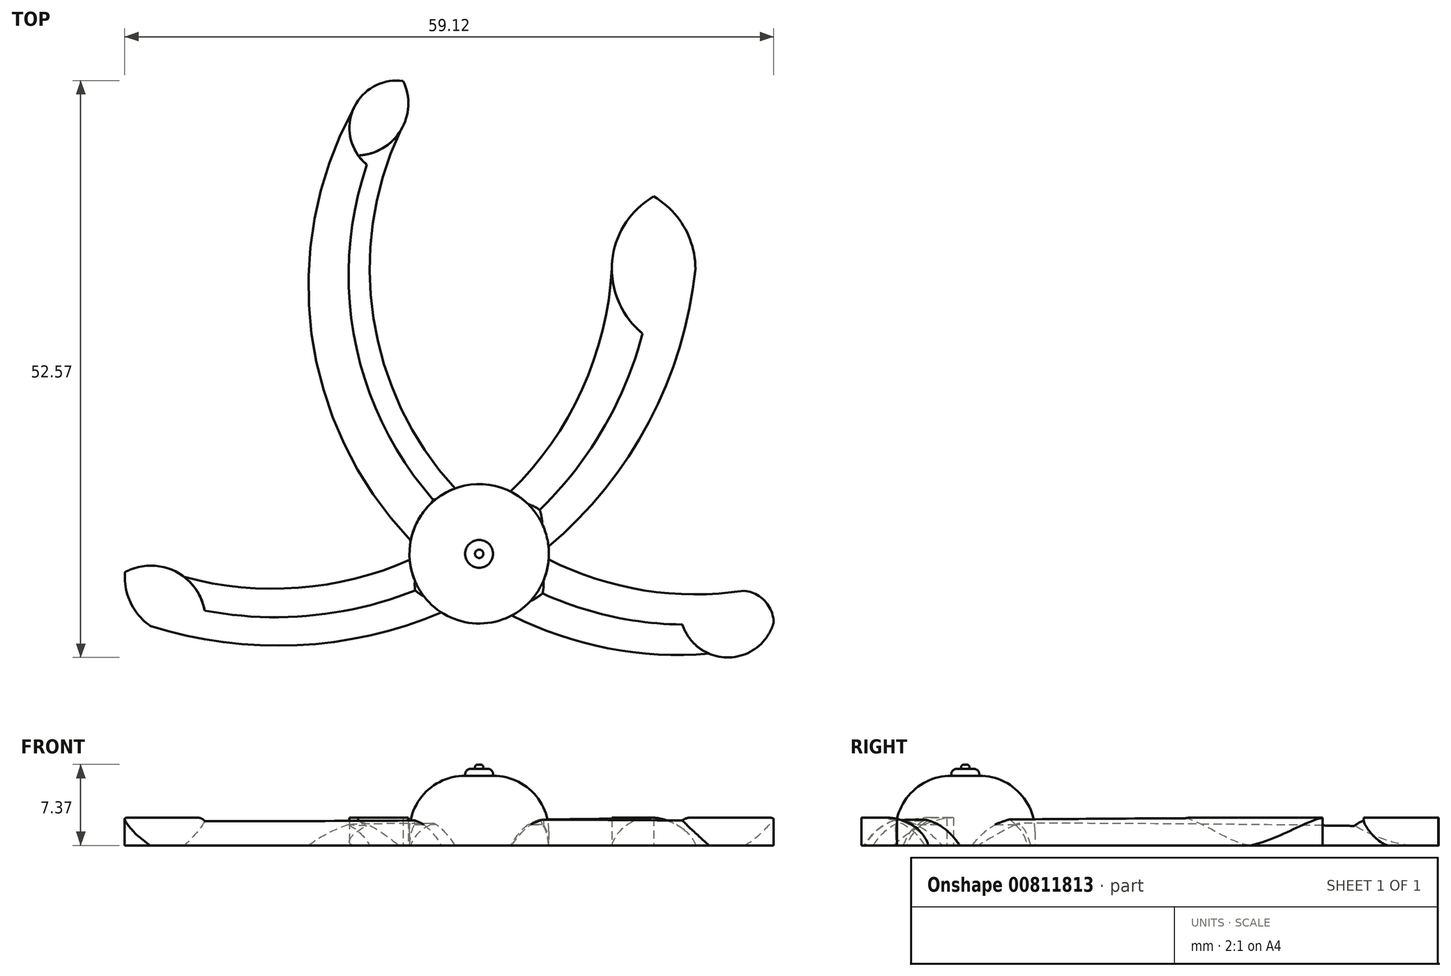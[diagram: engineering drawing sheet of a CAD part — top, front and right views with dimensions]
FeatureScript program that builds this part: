
annotation { "Feature Type Name" : "Feature", "Feature Type Description" : "" }
export const myFeature = defineFeature(function(context is Context, id is Id, definition is map)
    precondition{}
    {
        {
            var Q0;
            Q0=qCreatedBy(makeId("Top.planeOp"),FACE);
            var sketch = newSketch(context, id + "F0", { "sketchPlane" : qUnion([Q0])});
            skArc(sketch, "E0", {"start": v(-15.38, 23.36) * mm, "mid": v(-14.05, -11.17) * mm, "end": v(17, -26.35) * mm});
            skArc(sketch, "E1", {"start": v(-11.14, 21.25) * mm, "mid": v(-8.01, -9.06) * mm, "end": v(20.18, -20.62) * mm});
            skArc(sketch, "E2", {"start": v(-33.9, -23.82) * mm, "mid": v(-1.34, -19.37) * mm, "end": v(15.74, 8.71) * mm});
            skArc(sketch, "E3", {"start": v(-30.82, -19.37) * mm, "mid": v(-4.66, -14.6) * mm, "end": v(8.13, 8.71) * mm});
            skPoint(sketch, "E3.startSnap0", {"position": v(-1.34, -19.37) * mm});
            skCircle(sketch, "E4", {"center": v(-3.95, -17.25) * mm, "radius": 6.35 * mm});
            skLineSegment(sketch, "E5", {"start": v(-11.14, 21.25) * mm, "end": v(-15.38, 23.36) * mm});
            skLineSegment(sketch, "E6", {"start": v(8.13, 8.71) * mm, "end": v(15.74, 8.71) * mm});
            skLineSegment(sketch, "E7", {"start": v(20.18, -20.62) * mm, "end": v(17, -26.35) * mm});
            skLineSegment(sketch, "E8", {"start": v(-30.82, -19.37) * mm, "end": v(-33.9, -23.82) * mm});
            skLineSegment(sketch, "E9", {"start": v(11.94, 8.71) * mm, "end": v(11.94, 15.3) * mm});
            skArc(sketch, "E10", {"start": v(11.94, 15.3) * mm, "mid": v(9.15, 12.52) * mm, "end": v(8.13, 8.71) * mm});
            skArc(sketch, "E11", {"start": v(15.74, 8.71) * mm, "mid": v(14.72, 12.52) * mm, "end": v(11.94, 15.3) * mm});
            skLineSegment(sketch, "E12", {"start": v(-13.26, 22.3) * mm, "end": v(-10.87, 25.83) * mm});
            skArc(sketch, "E13", {"start": v(-10.87, 25.83) * mm, "mid": v(-13.53, 25.34) * mm, "end": v(-15.38, 23.36) * mm});
            skArc(sketch, "E14", {"start": v(-11.14, 21.25) * mm, "mid": v(-10.42, 23.5) * mm, "end": v(-10.87, 25.83) * mm});
            skLineSegment(sketch, "E15", {"start": v(-32.36, -21.6) * mm, "end": v(-36.22, -18.92) * mm});
            skArc(sketch, "E16", {"start": v(-36.22, -18.92) * mm, "mid": v(-35.72, -21.68) * mm, "end": v(-33.9, -23.82) * mm});
            skArc(sketch, "E17", {"start": v(-30.82, -19.37) * mm, "mid": v(-33.45, -18.35) * mm, "end": v(-36.22, -18.92) * mm});
            skLineSegment(sketch, "E18", {"start": v(18.58, -23.48) * mm, "end": v(22.88, -23.48) * mm});
            skArc(sketch, "E19", {"start": v(17, -26.35) * mm, "mid": v(20.59, -26.26) * mm, "end": v(22.88, -23.48) * mm});
            skArc(sketch, "E20", {"start": v(22.88, -23.48) * mm, "mid": v(22.06, -21.54) * mm, "end": v(20.18, -20.62) * mm});
            skSolve(sketch);
        }
        {
            var Q0;
            {var subQ0=sQuery(id+"F0.wireOp",EDGE,"E5");Q0=makeQuery(id+"F0.imprint","IMPRINT",FACE,{"disambiguationData":[TD([[makeQuery(id+"F0.imprint","IMPRINT",EDGE,{"derivedFrom":subQ0}),1.0]])]});}
            var Q1;
            {var subQ0=sQuery(id+"F0.wireOp",EDGE,"E7");Q1=makeQuery(id+"F0.imprint","IMPRINT",FACE,{"disambiguationData":[TD([[makeQuery(id+"F0.imprint","IMPRINT",EDGE,{"derivedFrom":subQ0}),-1.0]])]});}
            var Q2;
            {var subQ0=sQuery(id+"F0.wireOp",EDGE,"E8");Q2=makeQuery(id+"F0.imprint","IMPRINT",FACE,{"disambiguationData":[TD([[makeQuery(id+"F0.imprint","IMPRINT",EDGE,{"derivedFrom":subQ0}),1.0]])]});}
            var Q3;
            {var subQ0=sQuery(id+"F0.wireOp",EDGE,"E6");Q3=makeQuery(id+"F0.imprint","IMPRINT",FACE,{"disambiguationData":[TD([[makeQuery(id+"F0.imprint","IMPRINT",EDGE,{"derivedFrom":subQ0}),-1.0]])]});}
            var Q4;
            {var subQ2=sQuery(id+"F0.wireOp",EDGE,"E15");Q4=makeQuery(id+"F0.imprint","IMPRINT",FACE,{"disambiguationData":[TD([[makeQuery(id+"F0.imprint","IMPRINT",EDGE,{"derivedFrom":subQ2}),-1.0]])]});}
            var Q5;
            {var subQ2=sQuery(id+"F0.wireOp",EDGE,"E15");Q5=makeQuery(id+"F0.imprint","IMPRINT",FACE,{"disambiguationData":[TD([[makeQuery(id+"F0.imprint","IMPRINT",EDGE,{"derivedFrom":subQ2}),1.0]])]});}
            var Q6;
            {var subQ2=sQuery(id+"F0.wireOp",EDGE,"E12");Q6=makeQuery(id+"F0.imprint","IMPRINT",FACE,{"disambiguationData":[TD([[makeQuery(id+"F0.imprint","IMPRINT",EDGE,{"derivedFrom":subQ2}),1.0]])]});}
            var Q7;
            {var subQ2=sQuery(id+"F0.wireOp",EDGE,"E12");Q7=makeQuery(id+"F0.imprint","IMPRINT",FACE,{"disambiguationData":[TD([[makeQuery(id+"F0.imprint","IMPRINT",EDGE,{"derivedFrom":subQ2}),-1.0]])]});}
            var Q8;
            {var subQ2=sQuery(id+"F0.wireOp",EDGE,"E9");Q8=makeQuery(id+"F0.imprint","IMPRINT",FACE,{"disambiguationData":[TD([[makeQuery(id+"F0.imprint","IMPRINT",EDGE,{"derivedFrom":subQ2}),1.0]])]});}
            var Q9;
            {var subQ2=sQuery(id+"F0.wireOp",EDGE,"E9");Q9=makeQuery(id+"F0.imprint","IMPRINT",FACE,{"disambiguationData":[TD([[makeQuery(id+"F0.imprint","IMPRINT",EDGE,{"derivedFrom":subQ2}),-1.0]])]});}
            var Q10;
            {var subQ2=sQuery(id+"F0.wireOp",EDGE,"E18");Q10=makeQuery(id+"F0.imprint","IMPRINT",FACE,{"disambiguationData":[TD([[makeQuery(id+"F0.imprint","IMPRINT",EDGE,{"derivedFrom":subQ2}),1.0]])]});}
            var Q11;
            {var subQ2=sQuery(id+"F0.wireOp",EDGE,"E18");Q11=makeQuery(id+"F0.imprint","IMPRINT",FACE,{"disambiguationData":[TD([[makeQuery(id+"F0.imprint","IMPRINT",EDGE,{"derivedFrom":subQ2}),-1.0]])]});}
            extrude(context, id + "F1", {"entities" : qUnion([Q0, Q1, Q2, Q3, Q4, Q5, Q6, Q7, Q8, Q9, Q10, Q11]), "depth" : 2.54 * mm, "offsetDistance" : 25.4 * mm});
        }
        {
            var Q0;
            {var subQ0=sQuery(id+"F0.wireOp",EDGE,"E4");var subQ1=sQuery(id+"F0.wireOp",EDGE,"E0");var subQ2=makeQuery(id+"F0.imprint","INTERSECT",VERTEX,{"disambiguationData":[OD(0.0)],"derivedFrom":[subQ1,subQ0]});Q0=makeQuery(id+"F0.imprint","IMPRINT",FACE,{"disambiguationData":[TD([[makeQuery(id+"F0.imprint","IMPRINT",EDGE,{"disambiguationData":[TD([[subQ2,-1.0]])],"derivedFrom":subQ1}),1.0]])]});}
            var Q1;
            {var subQ0=sQuery(id+"F0.wireOp",EDGE,"E4");var subQ1=sQuery(id+"F0.wireOp",EDGE,"E0");var subQ2=makeQuery(id+"F0.imprint","INTERSECT",VERTEX,{"disambiguationData":[OD(0.0)],"derivedFrom":[subQ1,subQ0]});Q1=makeQuery(id+"F0.imprint","IMPRINT",FACE,{"disambiguationData":[TD([[makeQuery(id+"F0.imprint","IMPRINT",EDGE,{"disambiguationData":[TD([[subQ2,-1.0]])],"derivedFrom":subQ1}),-1.0]])]});}
            var Q2;
            {var subQ0=sQuery(id+"F0.wireOp",EDGE,"E4");var subQ1=sQuery(id+"F0.wireOp",EDGE,"E1");var subQ2=makeQuery(id+"F0.imprint","INTERSECT",VERTEX,{"disambiguationData":[OD(1.0)],"derivedFrom":[subQ1,subQ0]});Q2=makeQuery(id+"F0.imprint","IMPRINT",FACE,{"disambiguationData":[TD([[makeQuery(id+"F0.imprint","IMPRINT",EDGE,{"disambiguationData":[TD([[subQ2,1.0]])],"derivedFrom":subQ1}),1.0]])]});}
            var Q3;
            {var subQ0=sQuery(id+"F0.wireOp",EDGE,"E4");var subQ1=sQuery(id+"F0.wireOp",EDGE,"E0");var subQ2=makeQuery(id+"F0.imprint","INTERSECT",VERTEX,{"disambiguationData":[OD(1.0)],"derivedFrom":[subQ1,subQ0]});Q3=makeQuery(id+"F0.imprint","IMPRINT",FACE,{"disambiguationData":[TD([[makeQuery(id+"F0.imprint","IMPRINT",EDGE,{"disambiguationData":[TD([[subQ2,1.0]])],"derivedFrom":subQ1}),-1.0]])]});}
            var Q4;
            {var subQ0=sQuery(id+"F0.wireOp",EDGE,"E3");var subQ1=sQuery(id+"F0.wireOp",EDGE,"E0");var subQ2=makeQuery(id+"F0.imprint","INTERSECT",VERTEX,{"derivedFrom":[subQ1,subQ0]});Q4=makeQuery(id+"F0.imprint","IMPRINT",FACE,{"disambiguationData":[TD([[makeQuery(id+"F0.imprint","IMPRINT",EDGE,{"disambiguationData":[TD([[subQ2,-1.0]])],"derivedFrom":subQ1}),1.0]])]});}
            var Q5;
            {var subQ0=sQuery(id+"F0.wireOp",EDGE,"E3");var subQ1=sQuery(id+"F0.wireOp",EDGE,"E0");var subQ2=makeQuery(id+"F0.imprint","INTERSECT",VERTEX,{"derivedFrom":[subQ1,subQ0]});Q5=makeQuery(id+"F0.imprint","IMPRINT",FACE,{"disambiguationData":[TD([[makeQuery(id+"F0.imprint","IMPRINT",EDGE,{"disambiguationData":[TD([[subQ2,-1.0]])],"derivedFrom":subQ1}),-1.0]])]});}
            var Q6;
            {var subQ0=sQuery(id+"F0.wireOp",EDGE,"E4");var subQ1=sQuery(id+"F0.wireOp",EDGE,"E1");var subQ2=makeQuery(id+"F0.imprint","INTERSECT",VERTEX,{"disambiguationData":[OD(0.0)],"derivedFrom":[subQ1,subQ0]});Q6=makeQuery(id+"F0.imprint","IMPRINT",FACE,{"disambiguationData":[TD([[makeQuery(id+"F0.imprint","IMPRINT",EDGE,{"disambiguationData":[TD([[subQ2,-1.0]])],"derivedFrom":subQ1}),1.0]])]});}
            var Q7;
            {var subQ0=sQuery(id+"F0.wireOp",EDGE,"E3");var subQ1=sQuery(id+"F0.wireOp",EDGE,"E1");var subQ2=makeQuery(id+"F0.imprint","INTERSECT",VERTEX,{"derivedFrom":[subQ1,subQ0]});Q7=makeQuery(id+"F0.imprint","IMPRINT",FACE,{"disambiguationData":[TD([[makeQuery(id+"F0.imprint","IMPRINT",EDGE,{"disambiguationData":[TD([[subQ2,-1.0]])],"derivedFrom":subQ1}),1.0]])]});}
            var Q8;
            {var subQ0=sQuery(id+"F0.wireOp",EDGE,"E4");var subQ1=sQuery(id+"F0.wireOp",EDGE,"E0");var subQ2=makeQuery(id+"F0.imprint","INTERSECT",VERTEX,{"disambiguationData":[OD(1.0)],"derivedFrom":[subQ1,subQ0]});Q8=makeQuery(id+"F0.imprint","IMPRINT",FACE,{"disambiguationData":[TD([[makeQuery(id+"F0.imprint","IMPRINT",EDGE,{"disambiguationData":[TD([[subQ2,1.0]])],"derivedFrom":subQ1}),1.0]])]});}
            extrude(context, id + "F2", {"entities" : qUnion([Q0, Q1, Q2, Q3, Q4, Q5, Q6, Q7, Q8]), "depth" : 6.35 * mm, "offsetDistance" : 25.4 * mm});
        }
        {
            var Q0;
            Q0=makeQuery(id+"F2.opExtrude","CAP_EDGE",EDGE,{"disambiguationData":[OSD([sQuery(id+"F0.wireOp",EDGE,"E4")])],"isStart":false});
            fillet(context, id + "F3", {"entities" : qUnion([Q0]), "radius" : 5.08 * mm, "tangentPropagation" : true, "allowEdgeOverflow" : false});
        }
        {
            var Q0;
            {var subQ0=sQuery(id+"F0.wireOp",EDGE,"E4");Q0=makeQuery(id+"F1.opExtrude","CAP_EDGE",EDGE,{"disambiguationData":[OSD([subQ0]),TDD([makeQuery(id+"F0.imprint","IMPRINT",EDGE,{"disambiguationData":[TD([[makeQuery(id+"F0.imprint","INTERSECT",VERTEX,{"disambiguationData":[OD(0.0)],"derivedFrom":[sQuery(id+"F0.wireOp",EDGE,"E2"),subQ0]}),1.0]])],"derivedFrom":subQ0})])],"isStart":false});}
            chamfer(context, id + "F4", {"entities" : qUnion([Q0]), "width" : 0.64 * mm, "tangentPropagation" : true});
        }
        {
            var Q0;
            {var subQ0=sQuery(id+"F0.wireOp",EDGE,"E4");Q0=makeQuery(id+"F1.opExtrude","CAP_EDGE",EDGE,{"disambiguationData":[OSD([subQ0]),TDD([makeQuery(id+"F0.imprint","IMPRINT",EDGE,{"disambiguationData":[TD([[makeQuery(id+"F0.imprint","INTERSECT",VERTEX,{"disambiguationData":[OD(0.0)],"derivedFrom":[sQuery(id+"F0.wireOp",EDGE,"E0"),subQ0]}),1.0]])],"derivedFrom":subQ0})])],"isStart":false});}
            chamfer(context, id + "F5", {"entities" : qUnion([Q0]), "width" : 0.64 * mm, "tangentPropagation" : true});
        }
        {
            var Q0;
            {var subQ0=sQuery(id+"F0.wireOp",EDGE,"E4");Q0=makeQuery(id+"F1.opExtrude","CAP_EDGE",EDGE,{"disambiguationData":[OSD([subQ0]),TDD([makeQuery(id+"F0.imprint","IMPRINT",EDGE,{"disambiguationData":[TD([[makeQuery(id+"F0.imprint","INTERSECT",VERTEX,{"disambiguationData":[OD(1.0)],"derivedFrom":[sQuery(id+"F0.wireOp",EDGE,"E0"),subQ0]}),-1.0]])],"derivedFrom":subQ0})])],"isStart":false});}
            chamfer(context, id + "F6", {"entities" : qUnion([Q0]), "width" : 0.64 * mm, "tangentPropagation" : true});
        }
        {
            var Q0;
            {var subQ0=sQuery(id+"F0.wireOp",EDGE,"E4");Q0=makeQuery(id+"F1.opExtrude","CAP_EDGE",EDGE,{"disambiguationData":[OSD([subQ0]),TDD([makeQuery(id+"F0.imprint","IMPRINT",EDGE,{"disambiguationData":[TD([[makeQuery(id+"F0.imprint","INTERSECT",VERTEX,{"disambiguationData":[OD(1.0)],"derivedFrom":[sQuery(id+"F0.wireOp",EDGE,"E2"),subQ0]}),-1.0]])],"derivedFrom":subQ0})])],"isStart":false});}
            chamfer(context, id + "F7", {"entities" : qUnion([Q0]), "width" : 0.64 * mm, "tangentPropagation" : true});
        }
        {
            var Q0;
            {var subQ0=sQuery(id+"F0.wireOp",EDGE,"E3");Q0=makeQuery(id+"F1.opExtrude","CAP_EDGE",EDGE,{"disambiguationData":[OSD([subQ0]),TDD([makeQuery(id+"F0.imprint","IMPRINT",EDGE,{"disambiguationData":[TD([[makeQuery(id+"F0.imprint","INTERSECT",VERTEX,{"derivedFrom":[subQ0,sQuery(id+"F0.wireOp",EDGE,"E6")]}),1.0]])],"derivedFrom":subQ0})])],"isStart":false});}
            fillet(context, id + "F8", {"entities" : qUnion([Q0]), "radius" : 5.08 * mm, "tangentPropagation" : true, "allowEdgeOverflow" : false});
        }
        {
            var Q0;
            {var subQ0=sQuery(id+"F0.wireOp",EDGE,"E2");Q0=makeQuery(id+"F1.opExtrude","CAP_EDGE",EDGE,{"disambiguationData":[OSD([subQ0]),TDD([makeQuery(id+"F0.imprint","IMPRINT",EDGE,{"disambiguationData":[TD([[makeQuery(id+"F0.imprint","INTERSECT",VERTEX,{"derivedFrom":[subQ0,sQuery(id+"F0.wireOp",EDGE,"E6")]}),1.0]])],"derivedFrom":subQ0})])],"isStart":false});}
            fillet(context, id + "F9", {"entities" : qUnion([Q0]), "radius" : 5.08 * mm, "tangentPropagation" : true, "allowEdgeOverflow" : false});
        }
        {
            var Q0;
            {var subQ0=sQuery(id+"F0.wireOp",EDGE,"E1");Q0=makeQuery(id+"F1.opExtrude","CAP_EDGE",EDGE,{"disambiguationData":[OSD([subQ0]),TDD([makeQuery(id+"F0.imprint","IMPRINT",EDGE,{"disambiguationData":[TD([[makeQuery(id+"F0.imprint","INTERSECT",VERTEX,{"derivedFrom":[subQ0,sQuery(id+"F0.wireOp",EDGE,"E5")]}),-1.0]])],"derivedFrom":subQ0})])],"isStart":false});}
            fillet(context, id + "F10", {"entities" : qUnion([Q0]), "radius" : 5.08 * mm, "tangentPropagation" : true, "allowEdgeOverflow" : false});
        }
        {
            var Q0;
            {var subQ0=sQuery(id+"F0.wireOp",EDGE,"E3");Q0=makeQuery(id+"F1.opExtrude","CAP_EDGE",EDGE,{"disambiguationData":[OSD([subQ0]),TDD([makeQuery(id+"F0.imprint","IMPRINT",EDGE,{"disambiguationData":[TD([[makeQuery(id+"F0.imprint","INTERSECT",VERTEX,{"derivedFrom":[subQ0,sQuery(id+"F0.wireOp",EDGE,"E8")]}),-1.0]])],"derivedFrom":subQ0})])],"isStart":false});}
            fillet(context, id + "F11", {"entities" : qUnion([Q0]), "radius" : 5.08 * mm, "tangentPropagation" : true, "allowEdgeOverflow" : false});
        }
        {
            var Q0;
            {var subQ0=sQuery(id+"F0.wireOp",EDGE,"E2");Q0=makeQuery(id+"F1.opExtrude","CAP_EDGE",EDGE,{"disambiguationData":[OSD([subQ0]),TDD([makeQuery(id+"F0.imprint","IMPRINT",EDGE,{"disambiguationData":[TD([[makeQuery(id+"F0.imprint","INTERSECT",VERTEX,{"derivedFrom":[subQ0,sQuery(id+"F0.wireOp",EDGE,"E8")]}),-1.0]])],"derivedFrom":subQ0})])],"isStart":false});}
            fillet(context, id + "F12", {"entities" : qUnion([Q0]), "radius" : 5.08 * mm, "tangentPropagation" : true, "allowEdgeOverflow" : false});
        }
        {
            var Q0;
            {var subQ0=sQuery(id+"F0.wireOp",EDGE,"E0");Q0=makeQuery(id+"F1.opExtrude","CAP_EDGE",EDGE,{"disambiguationData":[OSD([subQ0]),TDD([makeQuery(id+"F0.imprint","IMPRINT",EDGE,{"disambiguationData":[TD([[makeQuery(id+"F0.imprint","INTERSECT",VERTEX,{"derivedFrom":[subQ0,sQuery(id+"F0.wireOp",EDGE,"E7")]}),1.0]])],"derivedFrom":subQ0})])],"isStart":false});}
            fillet(context, id + "F13", {"entities" : qUnion([Q0]), "radius" : 5.08 * mm, "tangentPropagation" : true, "allowEdgeOverflow" : false});
        }
        {
            var Q0;
            {var subQ0=sQuery(id+"F0.wireOp",EDGE,"E1");Q0=makeQuery(id+"F1.opExtrude","CAP_EDGE",EDGE,{"disambiguationData":[OSD([subQ0]),TDD([makeQuery(id+"F0.imprint","IMPRINT",EDGE,{"disambiguationData":[TD([[makeQuery(id+"F0.imprint","INTERSECT",VERTEX,{"derivedFrom":[subQ0,sQuery(id+"F0.wireOp",EDGE,"E7")]}),1.0]])],"derivedFrom":subQ0})])],"isStart":false});}
            fillet(context, id + "F14", {"entities" : qUnion([Q0]), "radius" : 5.08 * mm, "tangentPropagation" : true, "allowEdgeOverflow" : false});
        }
        {
            var Q0;
            {var subQ0=sQuery(id+"F0.wireOp",EDGE,"E0");Q0=makeQuery(id+"F1.opExtrude","CAP_EDGE",EDGE,{"disambiguationData":[OSD([subQ0]),TDD([makeQuery(id+"F0.imprint","IMPRINT",EDGE,{"disambiguationData":[TD([[makeQuery(id+"F0.imprint","INTERSECT",VERTEX,{"disambiguationData":[OD(0.0)],"derivedFrom":[subQ0,sQuery(id+"F0.wireOp",EDGE,"E4")]}),1.0]])],"derivedFrom":subQ0})])],"isStart":false});}
            fillet(context, id + "F15", {"entities" : qUnion([Q0]), "radius" : 12.7 * mm, "tangentPropagation" : true, "allowEdgeOverflow" : false});
        }
        {
            var Q0;
            Q0=makeQuery(id+"F2.opExtrude","CAP_FACE",FACE,{"disambiguationData":[OSD([sQuery(id+"F0.wireOp",EDGE,"E4")])],"isStart":false});
            extrude(context, id + "F16", {"entities" : qUnion([Q0]), "operationType" : NewBodyOperationType.ADD, "depth" : 0.64 * mm, "offsetDistance" : 25.4 * mm});
        }
        {
            var Q0;
            Q0=makeQuery(id+"F16.opExtrude","CAP_EDGE",EDGE,{"disambiguationData":[OSD([sQuery(id+"F0.wireOp",EDGE,"E4")])],"isStart":false});
            fillet(context, id + "F17", {"entities" : qUnion([Q0]), "radius" : 0.5 * mm, "tangentPropagation" : true, "allowEdgeOverflow" : false});
        }
        {
            var Q0;
            Q0=makeQuery(id+"F16.opExtrude","CAP_FACE",FACE,{"disambiguationData":[OSD([sQuery(id+"F0.wireOp",EDGE,"E4")])],"isStart":false});
            var sketch = newSketch(context, id + "F18", { "sketchPlane" : qUnion([Q0])});
            skCircle(sketch, "E21", {"center": v(-3.95, -17.25) * mm, "radius": 0.38 * mm});
            skSolve(sketch);
        }
        {
            var Q0;
            Q0=makeQuery(id+"F18.imprint","IMPRINT",FACE,{"disambiguationData":[TD([[makeQuery(id+"F18.imprint","IMPRINT",EDGE,{"derivedFrom":sQuery(id+"F18.wireOp",EDGE,"E21")}),1.0]])]});
            extrude(context, id + "F19", {"entities" : qUnion([Q0]), "operationType" : NewBodyOperationType.ADD, "depth" : 0.38 * mm, "offsetDistance" : 25.4 * mm});
        }
        {
            var Q0;
            Q0=makeQuery(id+"F19.opExtrude","CAP_EDGE",EDGE,{"disambiguationData":[OSD([sQuery(id+"F18.wireOp",EDGE,"E21")])],"isStart":false});
            fillet(context, id + "F20", {"entities" : qUnion([Q0]), "radius" : 0.25 * mm, "tangentPropagation" : true, "allowEdgeOverflow" : false});
        }
    });
